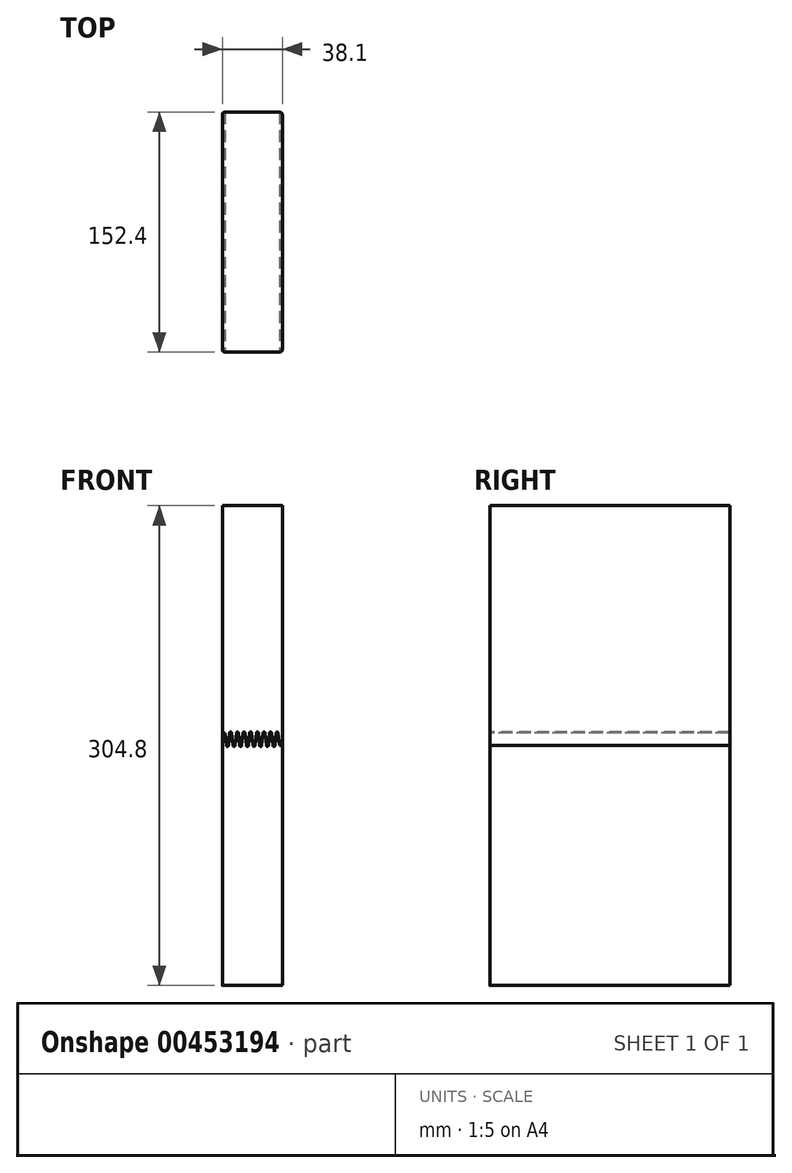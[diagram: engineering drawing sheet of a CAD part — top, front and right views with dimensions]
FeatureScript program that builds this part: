
annotation { "Feature Type Name" : "Feature", "Feature Type Description" : "" }
export const myFeature = defineFeature(function(context is Context, id is Id, definition is map)
    precondition{}
    {
        {
            var Q0;
            Q0=qCreatedBy(makeId("Front.planeOp"),FACE);
            var sketch = newSketch(context, id + "F0", { "sketchPlane" : qUnion([Q0])});
            skLineSegment(sketch, "E0.bottom", {"start": v(-38.1, 198.84) * mm, "end": v(0, 198.84) * mm});
            skLineSegment(sketch, "E0.top", {"start": v(-38.1, -105.96) * mm, "end": v(0, -105.96) * mm});
            skLineSegment(sketch, "E0.left", {"start": v(-38.1, 198.84) * mm, "end": v(-38.1, -105.96) * mm});
            skLineSegment(sketch, "E0.right", {"start": v(0, 198.84) * mm, "end": v(0, -105.96) * mm});
            skLineSegment(sketch, "E1.0", {"start": v(-37.66, 46.44) * mm, "end": v(4.94, 46.44) * mm, "construction": true});
            skLineSegment(sketch, "E2", {"start": v(27.89, 51.97) * mm, "end": v(27.89, 20.88) * mm});
            skLineSegment(sketch, "E3", {"start": v(27.89, 20.88) * mm, "end": v(30.71, 53.15) * mm});
            skLineSegment(sketch, "E4", {"start": v(41.42, 53.15) * mm, "end": v(41.42, 16.74) * mm});
            skLineSegment(sketch, "E5", {"start": v(41.42, 16.74) * mm, "end": v(46.06, 54.56) * mm});
            skLineSegment(sketch, "E6", {"start": v(27.89, 20.88) * mm, "end": v(25.09, 52.9) * mm});
            skLineSegment(sketch, "E7", {"start": v(41.42, 16.74) * mm, "end": v(36.89, 53.68) * mm});
            skLineSegment(sketch, "E8.0", {"start": v(-22.21, 198.32) * mm, "end": v(-22.21, -104.5) * mm, "construction": true});
            skArc(sketch, "E9", {"start": v(-22.84, 46.37) * mm, "mid": v(-22.21, 45.8) * mm, "end": v(-21.58, 46.37) * mm});
            skArc(sketch, "E10", {"start": v(-23.7, 54.51) * mm, "mid": v(-24.33, 55.08) * mm, "end": v(-24.96, 54.51) * mm});
            skArc(sketch, "E11", {"start": v(-19.46, 54.51) * mm, "mid": v(-20.1, 55.08) * mm, "end": v(-20.72, 54.51) * mm});
            skLineSegment(sketch, "E12", {"start": v(-23.7, 54.51) * mm, "end": v(-22.84, 46.37) * mm});
            skLineSegment(sketch, "E13", {"start": v(-21.58, 46.37) * mm, "end": v(-20.72, 54.51) * mm});
            skArc(sketch, "E14", {"start": v(-18.6, 46.37) * mm, "mid": v(-17.98, 45.8) * mm, "end": v(-17.34, 46.37) * mm});
            skArc(sketch, "E15", {"start": v(-14.38, 46.37) * mm, "mid": v(-13.75, 45.8) * mm, "end": v(-13.12, 46.37) * mm});
            skArc(sketch, "E16", {"start": v(-27.08, 46.37) * mm, "mid": v(-26.45, 45.8) * mm, "end": v(-25.82, 46.37) * mm});
            skArc(sketch, "E17", {"start": v(-31.3, 46.37) * mm, "mid": v(-30.67, 45.8) * mm, "end": v(-30.04, 46.37) * mm});
            skArc(sketch, "E18", {"start": v(-35.52, 46.37) * mm, "mid": v(-34.9, 45.8) * mm, "end": v(-34.26, 46.37) * mm});
            skArc(sketch, "E19", {"start": v(-27.93, 54.44) * mm, "mid": v(-28.56, 55.01) * mm, "end": v(-29.2, 54.44) * mm});
            skArc(sketch, "E20", {"start": v(-32.15, 54.44) * mm, "mid": v(-32.78, 55.01) * mm, "end": v(-33.41, 54.44) * mm});
            skArc(sketch, "E21", {"start": v(-15.23, 54.44) * mm, "mid": v(-15.86, 55.01) * mm, "end": v(-16.5, 54.44) * mm});
            skArc(sketch, "E22", {"start": v(-11, 54.44) * mm, "mid": v(-11.64, 55.01) * mm, "end": v(-12.27, 54.44) * mm});
            skLineSegment(sketch, "E23", {"start": v(-19.46, 54.51) * mm, "end": v(-18.6, 46.37) * mm});
            skLineSegment(sketch, "E24", {"start": v(-17.34, 46.37) * mm, "end": v(-16.5, 54.44) * mm});
            skLineSegment(sketch, "E25", {"start": v(-15.23, 54.44) * mm, "end": v(-14.38, 46.37) * mm});
            skLineSegment(sketch, "E26", {"start": v(-13.12, 46.37) * mm, "end": v(-12.27, 54.44) * mm});
            skLineSegment(sketch, "E27", {"start": v(-11, 54.44) * mm, "end": v(-10.16, 46.37) * mm});
            skLineSegment(sketch, "E28", {"start": v(-8.9, 46.37) * mm, "end": v(-8.05, 54.44) * mm});
            skLineSegment(sketch, "E29", {"start": v(-24.96, 54.51) * mm, "end": v(-25.82, 46.37) * mm});
            skLineSegment(sketch, "E30", {"start": v(-27.08, 46.37) * mm, "end": v(-27.93, 54.44) * mm});
            skLineSegment(sketch, "E31", {"start": v(-29.2, 54.44) * mm, "end": v(-30.04, 46.37) * mm});
            skLineSegment(sketch, "E32", {"start": v(-31.3, 46.37) * mm, "end": v(-32.15, 54.44) * mm});
            skLineSegment(sketch, "E33", {"start": v(-33.41, 54.44) * mm, "end": v(-34.26, 46.37) * mm});
            skArc(sketch, "E34", {"start": v(-5.94, 46.37) * mm, "mid": v(-5.3, 45.8) * mm, "end": v(-4.68, 46.37) * mm});
            skArc(sketch, "E35", {"start": v(-10.16, 46.37) * mm, "mid": v(-9.53, 45.8) * mm, "end": v(-8.9, 46.37) * mm});
            skArc(sketch, "E36", {"start": v(-2.56, 54.44) * mm, "mid": v(-3.2, 55.01) * mm, "end": v(-3.83, 54.44) * mm});
            skArc(sketch, "E37", {"start": v(-6.79, 54.44) * mm, "mid": v(-7.42, 55.01) * mm, "end": v(-8.05, 54.44) * mm});
            skLineSegment(sketch, "E38", {"start": v(-1.72, 46.44) * mm, "end": v(-2.56, 54.44) * mm});
            skLineSegment(sketch, "E39", {"start": v(-3.83, 54.44) * mm, "end": v(-4.68, 46.37) * mm});
            skLineSegment(sketch, "E40", {"start": v(-5.94, 46.37) * mm, "end": v(-6.79, 54.44) * mm});
            skPoint(sketch, "E41.orphan", {"position": v(-36.37, 54.44) * mm});
            skLineSegment(sketch, "E42", {"start": v(-36.37, 54.44) * mm, "end": v(-35.52, 46.37) * mm});
            skPoint(sketch, "E43.start.orphan", {"position": v(-10.16, 46.5) * mm});
            skPoint(sketch, "E44.center.orphan", {"position": v(-40.3, 46.44) * mm});
            skLineSegment(sketch, "E45", {"start": v(-1.72, 46.44) * mm, "end": v(0, 46.44) * mm});
            skLineSegment(sketch, "E46", {"start": v(-36.37, 54.44) * mm, "end": v(-38.1, 54.44) * mm});
            skSolve(sketch);
        }
        {
            var Q0;
            {var subQ1=sQuery(id+"F0.wireOp",EDGE,"E0.bottom");Q0=makeQuery(id+"F0.imprint","IMPRINT",FACE,{"disambiguationData":[TD([[makeQuery(id+"F0.imprint","IMPRINT",EDGE,{"derivedFrom":subQ1}),-1.0]])]});}
            extrude(context, id + "F1", {"entities" : qUnion([Q0]), "oppositeDirection" : true, "depth" : 152.4 * mm});
        }
        {
            var Q0;
            {var subQ1=sQuery(id+"F0.wireOp",EDGE,"E0.top");Q0=makeQuery(id+"F0.imprint","IMPRINT",FACE,{"disambiguationData":[TD([[makeQuery(id+"F0.imprint","IMPRINT",EDGE,{"derivedFrom":subQ1}),1.0]])]});}
            extrude(context, id + "F2", {"entities" : qUnion([Q0]), "oppositeDirection" : true, "depth" : 152.4 * mm});
        }
        {
            var Q0;
            Q0=makeQuery(id+"F1.opExtrude","CAP_EDGE",EDGE,{"disambiguationData":[OSD([sQuery(id+"F0.wireOp",EDGE,"E0.left")])],"isStart":true});
            var Q1;
            Q1=makeQuery(id+"F2.opExtrude","CAP_EDGE",EDGE,{"disambiguationData":[OSD([sQuery(id+"F0.wireOp",EDGE,"E0.left")])],"isStart":true});
            var Q2;
            Q2=makeQuery(id+"F1.opExtrude","CAP_EDGE",EDGE,{"disambiguationData":[OSD([sQuery(id+"F0.wireOp",EDGE,"E0.right")])],"isStart":true});
            var Q3;
            Q3=makeQuery(id+"F2.opExtrude","CAP_EDGE",EDGE,{"disambiguationData":[OSD([sQuery(id+"F0.wireOp",EDGE,"E0.right")])],"isStart":true});
            var Q4;
            Q4=makeQuery(id+"F2.opExtrude","CAP_EDGE",EDGE,{"disambiguationData":[OSD([sQuery(id+"F0.wireOp",EDGE,"E0.right")])],"isStart":false});
            var Q5;
            Q5=makeQuery(id+"F1.opExtrude","CAP_EDGE",EDGE,{"disambiguationData":[OSD([sQuery(id+"F0.wireOp",EDGE,"E0.right")])],"isStart":false});
            var Q6;
            Q6=makeQuery(id+"F1.opExtrude","CAP_EDGE",EDGE,{"disambiguationData":[OSD([sQuery(id+"F0.wireOp",EDGE,"E0.left")])],"isStart":false});
            var Q7;
            Q7=makeQuery(id+"F2.opExtrude","CAP_EDGE",EDGE,{"disambiguationData":[OSD([sQuery(id+"F0.wireOp",EDGE,"E0.left")])],"isStart":false});
            fillet(context, id + "F3", {"entities" : qUnion([Q0, Q1, Q2, Q3, Q4, Q5, Q6, Q7]), "radius" : 1.59 * mm, "tangentPropagation" : true, "allowEdgeOverflow" : false});
        }
    });
